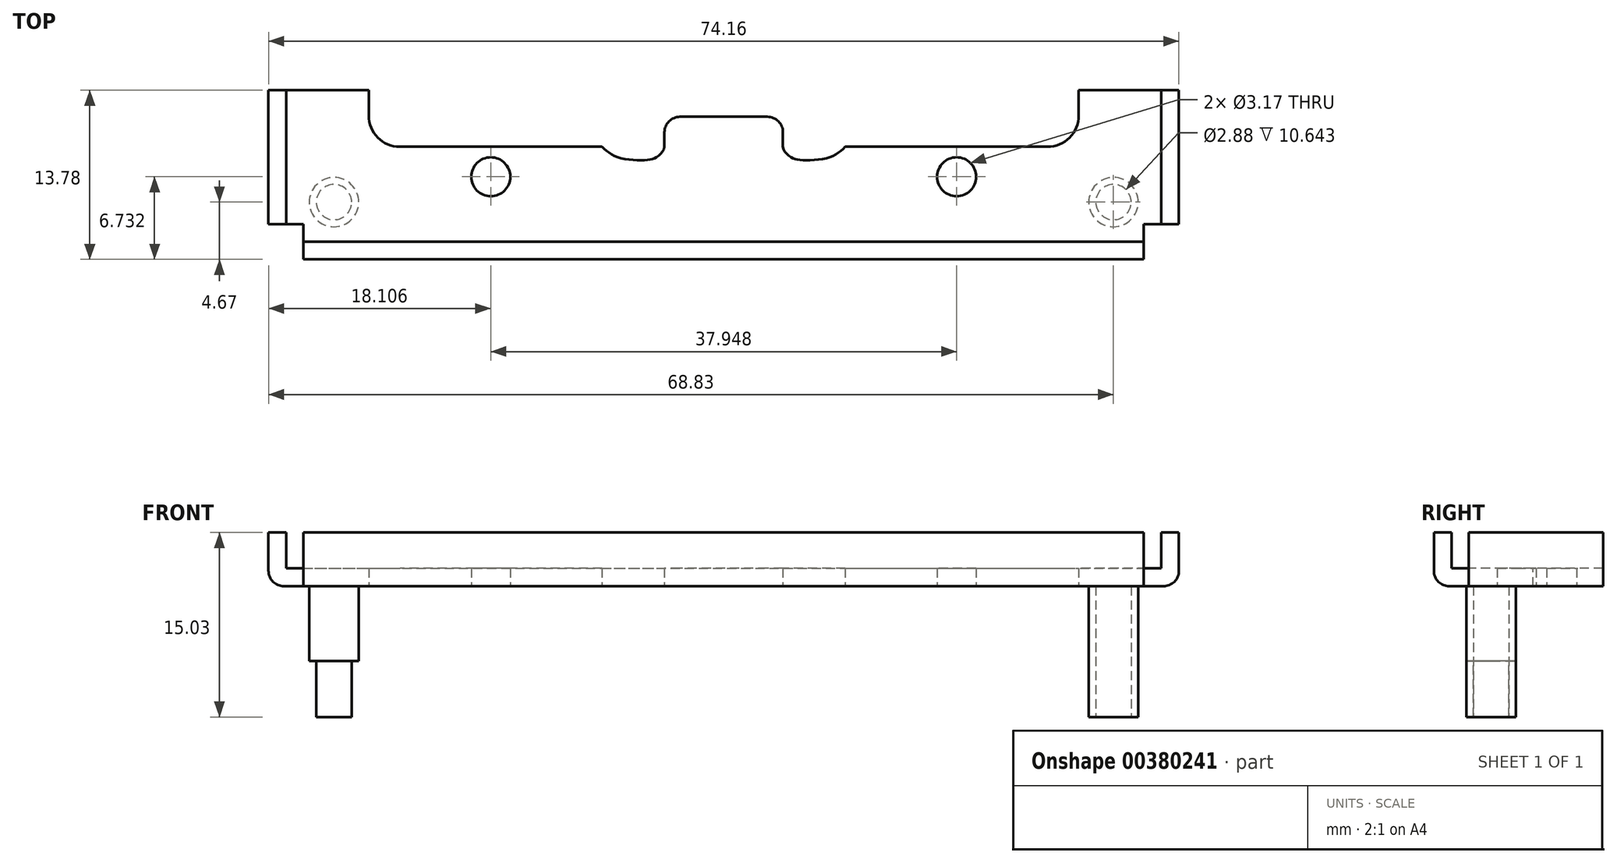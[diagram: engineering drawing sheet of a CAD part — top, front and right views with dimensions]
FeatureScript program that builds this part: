
annotation { "Feature Type Name" : "Feature", "Feature Type Description" : "" }
export const myFeature = defineFeature(function(context is Context, id is Id, definition is map)
    precondition{}
    {
        {
            var Q0;
            Q0=qCreatedBy(makeId("Top.planeOp"),FACE);
            var sketch = newSketch(context, id + "F0", { "sketchPlane" : qUnion([Q0])});
            skCircle(sketch, "E0", {"center": v(0, 0) * mm, "radius": 2.01 * mm});
            skCircle(sketch, "E1", {"center": v(0, 0) * mm, "radius": 1.44 * mm});
            skLineSegment(sketch, "E2", {"start": v(0, 0) * mm, "end": v(63.5, 0) * mm});
            skCircle(sketch, "E3.MirrorC", {"center": v(63.5, 0) * mm, "radius": 1.44 * mm});
            skCircle(sketch, "E4.MirrorC", {"center": v(63.5, 0) * mm, "radius": 2.01 * mm});
            skPoint(sketch, "E5.start.orphan", {"position": v(31.75, 0) * mm});
            skSolve(sketch);
        }
        {
            var Q0;
            Q0 = qSketchRegion(id + "F0", true);
            var Q1;
            Q1=makeQuery(id+"F0.imprint","IMPRINT",FACE,{"disambiguationData":[TD([[makeQuery(id+"F0.imprint","IMPRINT",EDGE,{"derivedFrom":sQuery(id+"F0.wireOp",EDGE,"E1")}),1.0]])]});
            var Q2;
            Q2=makeQuery(id+"F0.imprint","IMPRINT",FACE,{"disambiguationData":[TD([[makeQuery(id+"F0.imprint","IMPRINT",EDGE,{"derivedFrom":sQuery(id+"F0.wireOp",EDGE,"E3.MirrorC")}),-1.0]])]});
            extrude(context, id + "F1", {"entities" : qUnion([Q0, Q1, Q2]), "depth" : 6.1 * mm});
        }
        {
            var Q0;
            Q0=makeQuery(id+"F0.imprint","IMPRINT",FACE,{"disambiguationData":[TD([[makeQuery(id+"F0.imprint","IMPRINT",EDGE,{"derivedFrom":sQuery(id+"F0.wireOp",EDGE,"E3.MirrorC")}),-1.0]])]});
            var Q1;
            Q1=makeQuery(id+"F0.imprint","IMPRINT",FACE,{"disambiguationData":[TD([[makeQuery(id+"F0.imprint","IMPRINT",EDGE,{"derivedFrom":sQuery(id+"F0.wireOp",EDGE,"E1")}),1.0]])]});
            extrude(context, id + "F2", {"entities" : qUnion([Q0, Q1]), "operationType" : NewBodyOperationType.ADD, "oppositeDirection" : true, "depth" : 4.55 * mm});
        }
        {
            var Q0;
            Q0=makeQuery(id+"F1.opExtrude","CAP_FACE",FACE,{"disambiguationData":[OSD([sQuery(id+"F0.wireOp",EDGE,"E0")])],"isStart":false});
            var sketch = newSketch(context, id + "F3", { "sketchPlane" : qUnion([Q0])});
            skLineSegment(sketch, "E6", {"start": v(31.75, 0) * mm, "end": v(31.75, 23.76) * mm});
            skLineSegment(sketch, "E7.bottom", {"start": v(68.83, -4.67) * mm, "end": v(-5.33, -4.67) * mm});
            skLineSegment(sketch, "E7.top", {"start": v(68.83, 9.11) * mm, "end": v(60.67, 9.11) * mm});
            skLineSegment(sketch, "E7.left", {"start": v(68.83, -4.67) * mm, "end": v(68.83, 9.11) * mm});
            skLineSegment(sketch, "E7.right", {"start": v(-5.33, -4.67) * mm, "end": v(-5.33, 9.11) * mm});
            skPoint(sketch, "E7.middle", {"position": v(31.75, 2.22) * mm});
            skLineSegment(sketch, "E8", {"start": v(0, 0) * mm, "end": v(0, -4.67) * mm});
            skLineSegment(sketch, "E9.0", {"start": v(-3.89, -1.81) * mm, "end": v(-3.89, 9.11) * mm});
            skLineSegment(sketch, "E9.1", {"start": v(65.98, -3.22) * mm, "end": v(-2.48, -3.22) * mm});
            skLineSegment(sketch, "E9.2", {"start": v(67.39, -1.81) * mm, "end": v(67.39, 9.11) * mm});
            skLineSegment(sketch, "E10", {"start": v(-5.33, -4.67) * mm, "end": v(-2.48, -4.67) * mm});
            skLineSegment(sketch, "E11", {"start": v(-2.48, -4.67) * mm, "end": v(-2.48, -3.22) * mm});
            skLineSegment(sketch, "E12", {"start": v(-3.89, -1.81) * mm, "end": v(-5.33, -1.81) * mm});
            skLineSegment(sketch, "E13.MirrorCS", {"start": v(67.39, -1.81) * mm, "end": v(68.83, -1.81) * mm});
            skLineSegment(sketch, "E14.MirrorCS", {"start": v(65.98, -4.67) * mm, "end": v(65.98, -3.22) * mm});
            skPoint(sketch, "E15.orphan", {"position": v(65.98, -1.81) * mm});
            skPoint(sketch, "E16.orphan", {"position": v(-2.48, -1.81) * mm});
            skLineSegment(sketch, "E17", {"start": v(-5.33, 9.11) * mm, "end": v(2.83, 9.11) * mm});
            skLineSegment(sketch, "E18", {"start": v(12.78, 4.51) * mm, "end": v(12.78, -4.67) * mm});
            skLineSegment(sketch, "E19", {"start": v(12.78, -4.67) * mm, "end": v(12.78, 2.06) * mm});
            skPoint(sketch, "E19.endSnap0", {"position": v(12.78, 2.22) * mm});
            skCircle(sketch, "E20", {"center": v(12.78, 2.06) * mm, "radius": 1.59 * mm});
            skCircle(sketch, "E21.MirrorC", {"center": v(50.72, 2.06) * mm, "radius": 1.59 * mm});
            skLineSegment(sketch, "E22", {"start": v(26.92, 5.68) * mm, "end": v(26.92, 4.51) * mm});
            skLineSegment(sketch, "E23", {"start": v(2.83, 9.11) * mm, "end": v(2.83, 7.05) * mm});
            skLineSegment(sketch, "E24", {"start": v(21.84, 4.51) * mm, "end": v(5.37, 4.51) * mm});
            skPoint(sketch, "E25.visualSharp", {"position": v(2.83, 4.51) * mm});
            skArc(sketch, "E25.filletArc", {"start": v(2.83, 7.05) * mm, "mid": v(3.58, 5.26) * mm, "end": v(5.37, 4.51) * mm});
            skPoint(sketch, "E26.newPointA", {"position": v(26.92, 9.11) * mm});
            skPoint(sketch, "E26.newPointB", {"position": v(2.83, 9.11) * mm});
            skFitSpline(sketch, "E27", {"points": [v(21.84, 4.51) * mm, v(23.08, 3.66) * mm, v(25.37, 3.42) * mm, v(26.27, 3.66) * mm, v(26.92, 4.51) * mm], "startDerivative": vector(4.24, -3.92) * mm, "endDerivative": vector(0.48, 5.1) * mm});
            skLineSegment(sketch, "E28.MirrorCS", {"start": v(36.58, 5.68) * mm, "end": v(36.58, 4.51) * mm});
            skFitSpline(sketch, "E29.MirrorCS", {"points": [v(41.66, 4.51) * mm, v(40.42, 3.66) * mm, v(38.13, 3.42) * mm, v(37.23, 3.66) * mm, v(36.58, 4.51) * mm], "startDerivative": vector(-4.24, -3.92) * mm, "endDerivative": vector(-0.48, 5.1) * mm});
            skArc(sketch, "E30.MirrorCS", {"start": v(60.67, 7.05) * mm, "mid": v(59.92, 5.26) * mm, "end": v(58.13, 4.51) * mm});
            skLineSegment(sketch, "E31.MirrorCS", {"start": v(60.67, 9.11) * mm, "end": v(60.67, 7.05) * mm});
            skLineSegment(sketch, "E32.MirrorCS", {"start": v(41.66, 4.51) * mm, "end": v(58.13, 4.51) * mm});
            skLineSegment(sketch, "E33.trimOffspring", {"start": v(41.66, 4.51) * mm, "end": v(48.48, 4.51) * mm});
            skLineSegment(sketch, "E34.trimOffspring", {"start": v(2.83, 9.11) * mm, "end": v(-5.33, 9.11) * mm});
            skPoint(sketch, "E35.orphan", {"position": v(12.78, 9.11) * mm});
            skLineSegment(sketch, "E36", {"start": v(-2.48, -3.22) * mm, "end": v(-2.48, -1.81) * mm});
            skLineSegment(sketch, "E37", {"start": v(-3.89, -1.81) * mm, "end": v(-2.48, -1.81) * mm});
            skLineSegment(sketch, "E38", {"start": v(65.98, -3.22) * mm, "end": v(65.98, -1.81) * mm});
            skLineSegment(sketch, "E39", {"start": v(67.39, -1.81) * mm, "end": v(65.98, -1.81) * mm});
            skLineSegment(sketch, "E40.0", {"start": v(35.3, 6.95) * mm, "end": v(28.2, 6.95) * mm});
            skLineSegment(sketch, "E41", {"start": v(35.3, 6.95) * mm, "end": v(35.3, 6.95) * mm});
            skLineSegment(sketch, "E42", {"start": v(28.2, 6.95) * mm, "end": v(28.2, 6.95) * mm});
            skPoint(sketch, "E43.MirrorCS.end.orphan", {"position": v(36.58, 7.84) * mm});
            skPoint(sketch, "E44.MirrorCS.end.orphan", {"position": v(35.3, 9.11) * mm});
            skPoint(sketch, "E44.MirrorCS.start.orphan", {"position": v(31.75, 9.11) * mm});
            skPoint(sketch, "E45.trimOffspring.end.orphan", {"position": v(28.2, 9.11) * mm});
            skPoint(sketch, "E46.orphan", {"position": v(26.92, 7.84) * mm});
            skPoint(sketch, "E47.visualSharp", {"position": v(26.92, 6.95) * mm});
            skArc(sketch, "E47.filletArc", {"start": v(28.2, 6.95) * mm, "mid": v(27.3, 6.58) * mm, "end": v(26.92, 5.68) * mm});
            skPoint(sketch, "E48.visualSharp", {"position": v(36.58, 6.95) * mm});
            skArc(sketch, "E48.filletArc", {"start": v(36.58, 5.68) * mm, "mid": v(36.2, 6.58) * mm, "end": v(35.3, 6.95) * mm});
            skSolve(sketch);
        }
        {
            var Q0;
            Q0=makeQuery(id+"F3.imprint","IMPRINT",FACE,{"disambiguationData":[TD([[makeQuery(id+"F3.imprint","IMPRINT",EDGE,{"derivedFrom":makeQuery(id+"F1.opExtrude","CAP_EDGE",EDGE,{"disambiguationData":[OSD([sQuery(id+"F0.wireOp",EDGE,"E0")])],"isStart":false})}),1.0]])]});
            var Q1;
            {var subQ3=sQuery(id+"F3.wireOp",EDGE,"E9.2");Q1=makeQuery(id+"F3.imprint","IMPRINT",FACE,{"disambiguationData":[TD([[makeQuery(id+"F3.imprint","IMPRINT",EDGE,{"derivedFrom":subQ3}),-1.0]])]});}
            var Q2;
            {var subQ4=sQuery(id+"F3.wireOp",EDGE,"E9.0");Q2=makeQuery(id+"F3.imprint","IMPRINT",FACE,{"disambiguationData":[TD([[makeQuery(id+"F3.imprint","IMPRINT",EDGE,{"derivedFrom":subQ4}),1.0]])]});}
            var Q3;
            {var subQ0=sQuery(id+"F3.wireOp",EDGE,"E14.MirrorCS");Q3=makeQuery(id+"F3.imprint","IMPRINT",FACE,{"disambiguationData":[TD([[makeQuery(id+"F3.imprint","IMPRINT",EDGE,{"derivedFrom":subQ0}),1.0]])]});}
            var Q4;
            {var subQ0=sQuery(id+"F3.wireOp",EDGE,"E8");var subQ1=sQuery(id+"F3.wireOp",EDGE,"E7.bottom");var subQ2=makeQuery(id+"F3.imprint","INTERSECT",VERTEX,{"derivedFrom":[subQ1,subQ0]});Q4=makeQuery(id+"F3.imprint","IMPRINT",FACE,{"disambiguationData":[TD([[makeQuery(id+"F3.imprint","IMPRINT",EDGE,{"disambiguationData":[TD([[subQ2,1.0]])],"derivedFrom":subQ1}),-1.0]])]});}
            var Q5;
            {var subQ0=sQuery(id+"F3.wireOp",EDGE,"E11");Q5=makeQuery(id+"F3.imprint","IMPRINT",FACE,{"disambiguationData":[TD([[makeQuery(id+"F3.imprint","IMPRINT",EDGE,{"derivedFrom":subQ0}),-1.0]])]});}
            var Q6;
            {var subQ6=sQuery(id+"F3.wireOp",EDGE,"E9.2");Q6=makeQuery(id+"F3.imprint","IMPRINT",FACE,{"disambiguationData":[TD([[makeQuery(id+"F3.imprint","IMPRINT",EDGE,{"derivedFrom":subQ6}),1.0]])]});}
            var Q7;
            {var subQ7=sQuery(id+"F3.wireOp",EDGE,"E9.0");Q7=makeQuery(id+"F3.imprint","IMPRINT",FACE,{"disambiguationData":[TD([[makeQuery(id+"F3.imprint","IMPRINT",EDGE,{"derivedFrom":subQ7}),-1.0]])]});}
            extrude(context, id + "F4", {"entities" : qUnion([Q0, Q1, Q2, Q3, Q4, Q5, Q6, Q7]), "operationType" : NewBodyOperationType.ADD, "depth" : 1.47 * mm});
        }
        {
            var Q0;
            {var subQ4=sQuery(id+"F3.wireOp",EDGE,"E9.0");Q0=makeQuery(id+"F3.imprint","IMPRINT",FACE,{"disambiguationData":[TD([[makeQuery(id+"F3.imprint","IMPRINT",EDGE,{"derivedFrom":subQ4}),1.0]])]});}
            var Q1;
            {var subQ0=sQuery(id+"F3.wireOp",EDGE,"E8");var subQ1=sQuery(id+"F3.wireOp",EDGE,"E7.bottom");var subQ2=makeQuery(id+"F3.imprint","INTERSECT",VERTEX,{"derivedFrom":[subQ1,subQ0]});Q1=makeQuery(id+"F3.imprint","IMPRINT",FACE,{"disambiguationData":[TD([[makeQuery(id+"F3.imprint","IMPRINT",EDGE,{"disambiguationData":[TD([[subQ2,1.0]])],"derivedFrom":subQ1}),-1.0]])]});}
            var Q2;
            {var subQ0=sQuery(id+"F3.wireOp",EDGE,"E14.MirrorCS");Q2=makeQuery(id+"F3.imprint","IMPRINT",FACE,{"disambiguationData":[TD([[makeQuery(id+"F3.imprint","IMPRINT",EDGE,{"derivedFrom":subQ0}),1.0]])]});}
            var Q3;
            {var subQ3=sQuery(id+"F3.wireOp",EDGE,"E9.2");Q3=makeQuery(id+"F3.imprint","IMPRINT",FACE,{"disambiguationData":[TD([[makeQuery(id+"F3.imprint","IMPRINT",EDGE,{"derivedFrom":subQ3}),-1.0]])]});}
            var Q4;
            {var subQ0=sQuery(id+"F3.wireOp",EDGE,"E11");Q4=makeQuery(id+"F3.imprint","IMPRINT",FACE,{"disambiguationData":[TD([[makeQuery(id+"F3.imprint","IMPRINT",EDGE,{"derivedFrom":subQ0}),-1.0]])]});}
            extrude(context, id + "F5", {"entities" : qUnion([Q0, Q1, Q2, Q3, Q4]), "operationType" : NewBodyOperationType.ADD, "depth" : 4.38 * mm});
        }
        {
            var Q0;
            Q0=makeQuery(id+"F4.opExtrude","CAP_EDGE",EDGE,{"disambiguationData":[OSD([sQuery(id+"F3.wireOp",EDGE,"E7.right")])],"isStart":true});
            var Q1;
            Q1=makeQuery(id+"F4.opExtrude","CAP_EDGE",EDGE,{"disambiguationData":[OSD([sQuery(id+"F3.wireOp",EDGE,"E7.bottom")])],"isStart":true});
            var Q2;
            Q2=makeQuery(id+"F4.opExtrude","CAP_EDGE",EDGE,{"disambiguationData":[OSD([sQuery(id+"F3.wireOp",EDGE,"E7.left")])],"isStart":true});
            fillet(context, id + "F6", {"entities" : qUnion([Q0, Q1, Q2]), "radius" : 1.27 * mm, "tangentPropagation" : true, "allowEdgeOverflow" : false});
        }
    });
